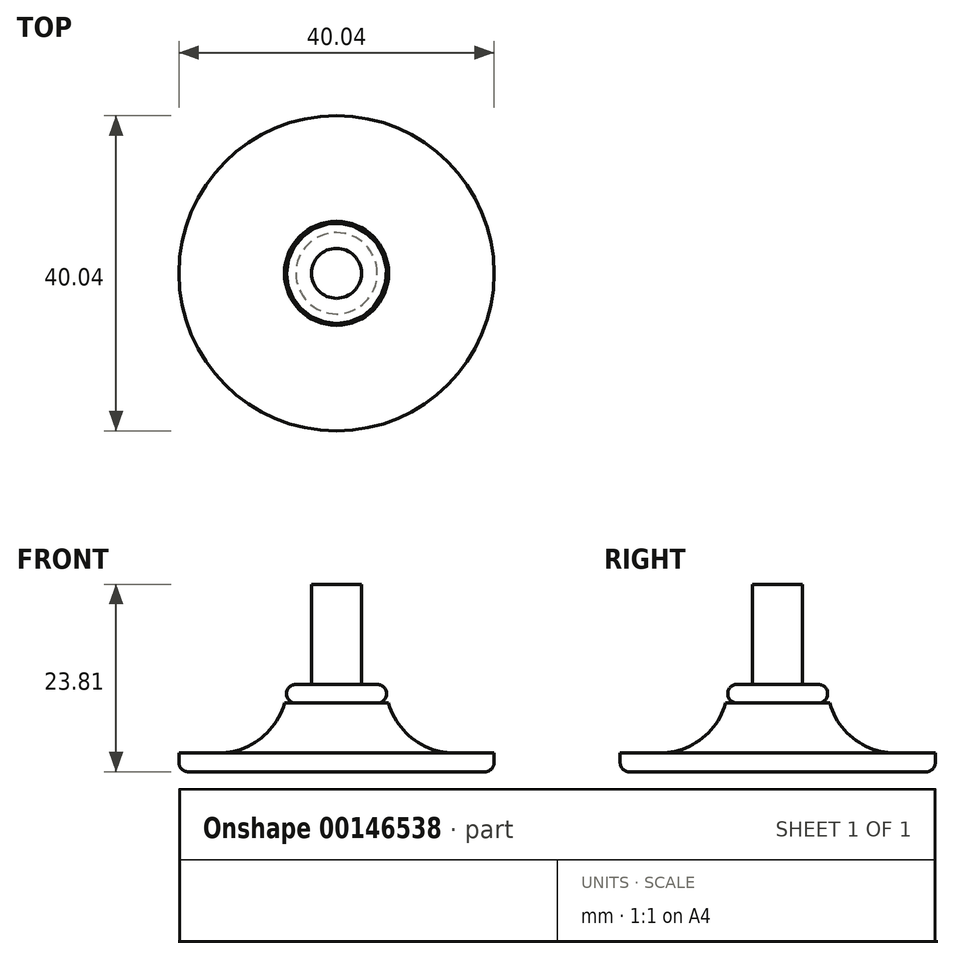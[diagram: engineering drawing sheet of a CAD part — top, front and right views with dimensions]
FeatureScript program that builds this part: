
annotation { "Feature Type Name" : "Feature", "Feature Type Description" : "" }
export const myFeature = defineFeature(function(context is Context, id is Id, definition is map)
    precondition{}
    {
        {
            var Q0;
            Q0=qCreatedBy(makeId("Front.planeOp"),FACE);
            var sketch = newSketch(context, id + "F0", { "sketchPlane" : qUnion([Q0])});
            skLineSegment(sketch, "E0", {"start": v(0, 0) * mm, "end": v(18.83, 0) * mm});
            skLineSegment(sketch, "E1", {"start": v(20.02, 2.38) * mm, "end": v(15, 2.38) * mm});
            skLineSegment(sketch, "E2", {"start": v(0, 0) * mm, "end": v(0, 23.81) * mm});
            skLineSegment(sketch, "E3", {"start": v(0, 23.81) * mm, "end": v(3.17, 23.81) * mm});
            skLineSegment(sketch, "E4", {"start": v(3.17, 23.81) * mm, "end": v(3.17, 11.11) * mm});
            skLineSegment(sketch, "E5", {"start": v(3.17, 11.11) * mm, "end": v(5.16, 11.11) * mm});
            skLineSegment(sketch, "E6", {"start": v(5.16, 8.73) * mm, "end": v(6.6, 8.73) * mm});
            skArc(sketch, "E7", {"start": v(5.16, 11.11) * mm, "mid": v(6.35, 9.92) * mm, "end": v(5.16, 8.73) * mm});
            skArc(sketch, "E8", {"start": v(15, 2.38) * mm, "mid": v(9.74, 4.15) * mm, "end": v(6.6, 8.73) * mm});
            skLineSegment(sketch, "E9", {"start": v(20.02, 2.38) * mm, "end": v(20.02, 1.2) * mm});
            skArc(sketch, "E10", {"start": v(20.02, 1.2) * mm, "mid": v(19.67, 0.35) * mm, "end": v(18.83, 0) * mm});
            skLineSegment(sketch, "E11", {"start": v(18.83, 2.38) * mm, "end": v(18.83, 0) * mm, "construction": true});
            skSolve(sketch);
        }
        {
            var Q0;
            Q0=makeQuery(id+"F0.imprint","IMPRINT",FACE,{"disambiguationData":[TD([[makeQuery(id+"F0.imprint","IMPRINT",EDGE,{"derivedFrom":sQuery(id+"F0.wireOp",EDGE,"E0")}),1.0]])]});
            var Q1;
            Q1=sQuery(id+"F0.wireOp",EDGE,"E2");
            revolve(context, id + "F1", {"entities" : qUnion([Q0]), "axis" : qUnion([Q1]), "revolveType" : RevolveType.FULL});
        }
    });
